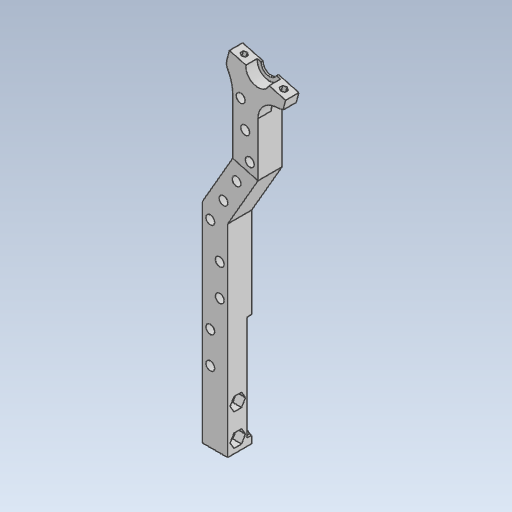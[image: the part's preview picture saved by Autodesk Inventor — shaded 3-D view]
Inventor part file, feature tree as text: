
AUTODESK INVENTOR PART (.ipt)
format: ipt  version: 2021.2 (Build 252289000, 289)  size: 311,808 bytes
history: native  units: mm
features: other x10, fillet x1, chamfer x1
ambient origin geometry x8: Origin, YZ Plane, XZ Plane, XY Plane, X Axis, Y Axis, Z Axis, Center Point
bodies: Body1 (feature_tree), Body2 (feature_tree)
feature tree (12):
  other  "Твёрдое тело.ipt"
  other  "РабПлоскость1"
  other  "Разделение1"
  fillet  "Сопряжение1"  Radius=10.0mm
  chamfer  "Фаска1"  Distance=2.0mm
  other  "Ножка 1::Твёрдое тело.ipt"
  other  "Элемент создания тегов1"
  other  "Ножка правая верх::Твёрдое тело.ipt"
  other  "Ножка правая низ::Твёрдое тело.ipt"
  other  "Твердое тело1"
  other  "Твердое тело2"
  other  "Твердое тело3"
